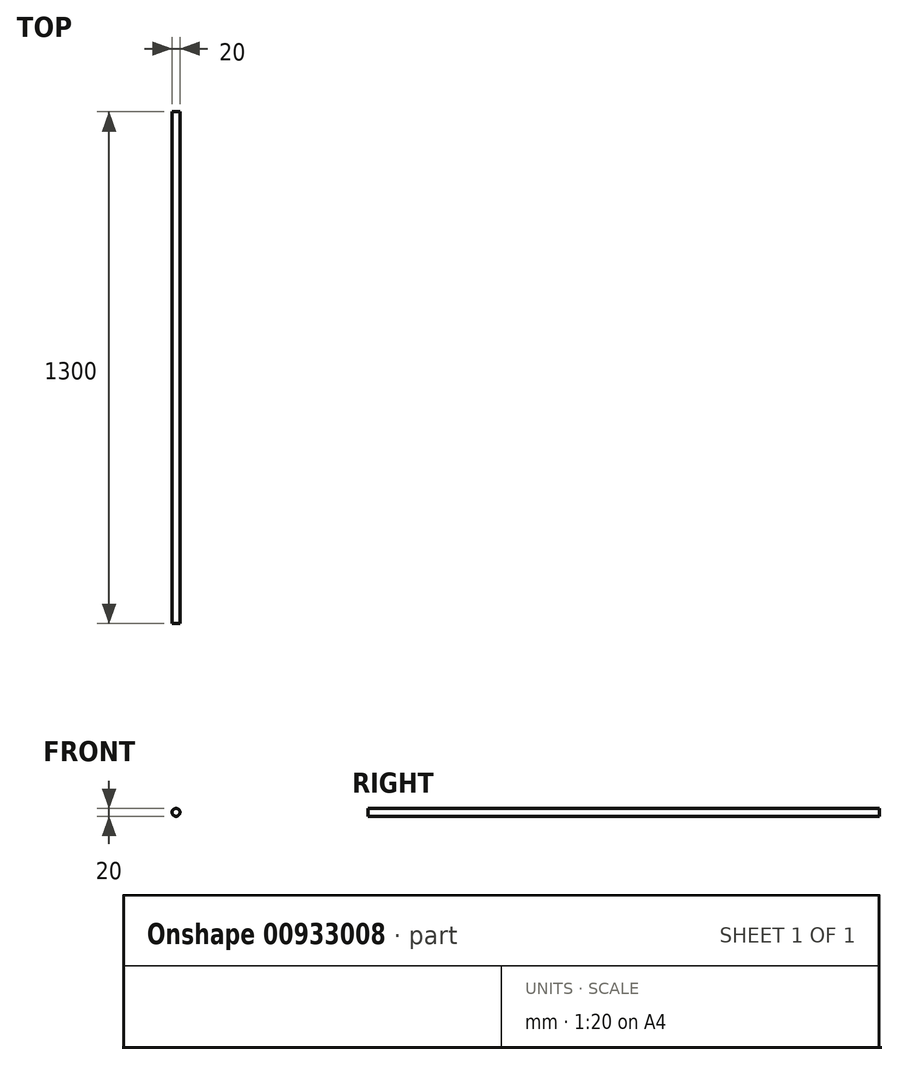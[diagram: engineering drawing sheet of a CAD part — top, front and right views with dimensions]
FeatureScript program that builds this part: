
annotation { "Feature Type Name" : "Feature", "Feature Type Description" : "" }
export const myFeature = defineFeature(function(context is Context, id is Id, definition is map)
    precondition{}
    {
        {
            var Q0;
            Q0=qCreatedBy(makeId("Front.planeOp"),FACE);
            var sketch = newSketch(context, id + "F0", { "sketchPlane" : qUnion([Q0])});
            skCircle(sketch, "E0", {"center": v(0, 0) * mm, "radius": 10 * mm});
            skSolve(sketch);
        }
        {
            var Q0;
            Q0 = qSketchRegion(id + "F0", true);
            extrude(context, id + "F1", {"entities" : qUnion([Q0]), "depth" : 1300 * mm, "offsetDistance" : 25 * mm});
        }
    });
